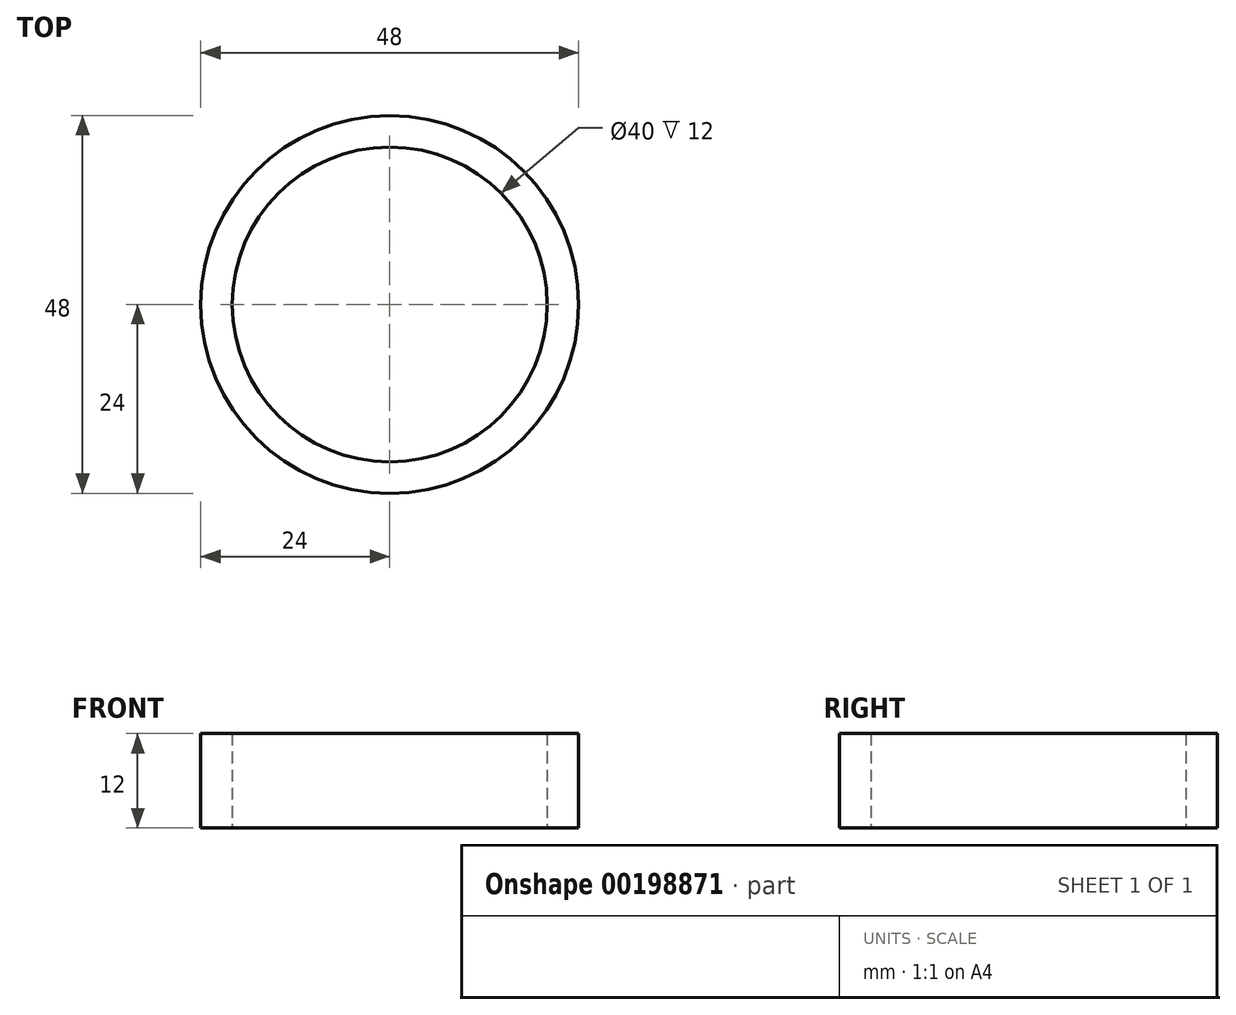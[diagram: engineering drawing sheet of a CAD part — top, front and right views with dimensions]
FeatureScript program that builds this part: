
annotation { "Feature Type Name" : "Feature", "Feature Type Description" : "" }
export const myFeature = defineFeature(function(context is Context, id is Id, definition is map)
    precondition{}
    {
        {
            var Q0;
            Q0=qCreatedBy(makeId("Top.planeOp"),FACE);
            var sketch = newSketch(context, id + "F0", { "sketchPlane" : qUnion([Q0])});
            skCircle(sketch, "E0", {"center": v(0, 0) * mm, "radius": 20 * mm});
            skCircle(sketch, "E1", {"center": v(0, 0) * mm, "radius": 24 * mm});
            skSolve(sketch);
        }
        {
            var Q0;
            Q0=makeQuery(id+"F0.imprint","IMPRINT",FACE,{"disambiguationData":[TD([[makeQuery(id+"F0.imprint","IMPRINT",EDGE,{"derivedFrom":sQuery(id+"F0.wireOp",EDGE,"E0")}),-1.0]])]});
            extrude(context, id + "F1", {"entities" : qUnion([Q0]), "depth" : 12 * mm});
        }
    });
